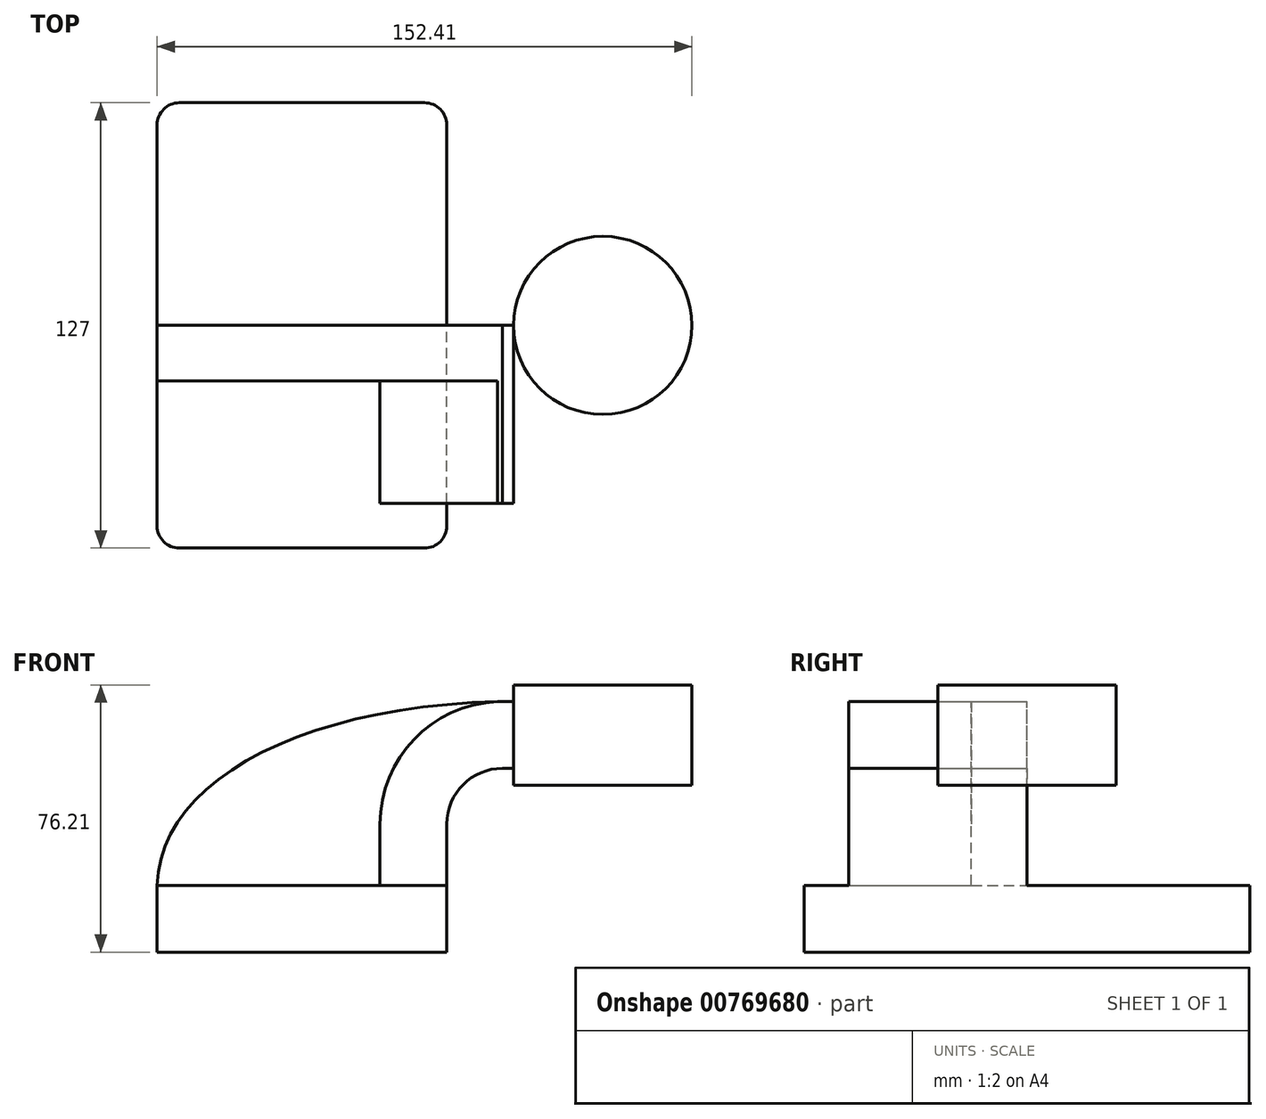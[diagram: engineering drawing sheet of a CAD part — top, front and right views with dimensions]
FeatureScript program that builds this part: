
annotation { "Feature Type Name" : "Feature", "Feature Type Description" : "" }
export const myFeature = defineFeature(function(context is Context, id is Id, definition is map)
    precondition{}
    {
        {
            var Q0;
            Q0=qCreatedBy(makeId("Front.planeOp"),FACE);
            var sketch = newSketch(context, id + "F0", { "sketchPlane" : qUnion([Q0])});
            skLineSegment(sketch, "E0.bottom", {"start": v(41.27, 9.53) * mm, "end": v(-41.28, 9.53) * mm});
            skLineSegment(sketch, "E0.top", {"start": v(41.28, -9.52) * mm, "end": v(-41.27, -9.52) * mm});
            skLineSegment(sketch, "E0.left", {"start": v(41.28, 9.53) * mm, "end": v(41.28, -9.52) * mm});
            skLineSegment(sketch, "E0.right", {"start": v(-41.28, 9.53) * mm, "end": v(-41.27, -9.52) * mm});
            skPoint(sketch, "E0.middle", {"position": v(0, 0) * mm});
            skLineSegment(sketch, "E1", {"start": v(41.27, 9.53) * mm, "end": v(41.27, 27) * mm});
            skArc(sketch, "E2", {"start": v(41.27, 27) * mm, "mid": v(45.92, 38.23) * mm, "end": v(57.15, 42.88) * mm});
            skLineSegment(sketch, "E3", {"start": v(57.15, 42.88) * mm, "end": v(85.72, 42.88) * mm});
            skLineSegment(sketch, "E4.bottom", {"start": v(111.12, 38.1) * mm, "end": v(60.33, 38.1) * mm});
            skLineSegment(sketch, "E4.top", {"start": v(111.12, 66.68) * mm, "end": v(60.33, 66.68) * mm});
            skLineSegment(sketch, "E4.left", {"start": v(111.12, 38.1) * mm, "end": v(111.12, 66.68) * mm});
            skLineSegment(sketch, "E4.right", {"start": v(60.33, 38.1) * mm, "end": v(60.33, 66.68) * mm});
            skPoint(sketch, "E4.middle", {"position": v(85.73, 52.39) * mm});
            skLineSegment(sketch, "E5.0", {"start": v(57.15, 61.93) * mm, "end": v(85.72, 61.93) * mm});
            skArc(sketch, "E5.1", {"start": v(22.23, 27) * mm, "mid": v(32.45, 51.7) * mm, "end": v(57.15, 61.93) * mm});
            skLineSegment(sketch, "E5.2", {"start": v(22.22, 9.53) * mm, "end": v(22.22, 27) * mm});
            skLineSegment(sketch, "E6", {"start": v(85.72, 38.1) * mm, "end": v(85.72, 66.68) * mm});
            skFitSpline(sketch, "E7", {"points": [v(-41.28, 9.53) * mm, v(57.15, 61.93) * mm], "startDerivative": vector(2.07, 88.8) * mm, "endDerivative": vector(171.45, 3.03) * mm});
            skSolve(sketch);
        }
        {
            var Q0;
            Q0=makeQuery(id+"F0.imprint","IMPRINT",FACE,{"disambiguationData":[TD([[makeQuery(id+"F0.imprint","IMPRINT",EDGE,{"derivedFrom":sQuery(id+"F0.wireOp",EDGE,"E0.top")}),-1.0]])]});
            extrude(context, id + "F1", {"entities" : qUnion([Q0]), "endBound" : BoundingType.SYMMETRIC, "depth" : 127 * mm, "offsetDistance" : 25.4 * mm});
        }
        {
            var Q0;
            {var subQ9=sQuery(id+"F0.wireOp",EDGE,"E1");Q0=makeQuery(id+"F0.imprint","IMPRINT",FACE,{"disambiguationData":[TD([[makeQuery(id+"F0.imprint","IMPRINT",EDGE,{"derivedFrom":subQ9}),1.0]])]});}
            extrude(context, id + "F2", {"entities" : qUnion([Q0]), "operationType" : NewBodyOperationType.ADD, "depth" : 50.8 * mm, "offsetDistance" : 25.4 * mm});
        }
        {
            var Q0;
            {var subQ3=sQuery(id+"F0.wireOp",EDGE,"E5.2");Q0=makeQuery(id+"F0.imprint","IMPRINT",FACE,{"disambiguationData":[TD([[makeQuery(id+"F0.imprint","IMPRINT",EDGE,{"derivedFrom":subQ3}),1.0]])]});}
            extrude(context, id + "F3", {"entities" : qUnion([Q0]), "operationType" : NewBodyOperationType.ADD, "depth" : 15.88 * mm, "offsetDistance" : 25.4 * mm});
        }
        {
            var Q0;
            {var subQ4=sQuery(id+"F0.wireOp",EDGE,"E4.left");Q0=makeQuery(id+"F0.imprint","IMPRINT",FACE,{"disambiguationData":[TD([[makeQuery(id+"F0.imprint","IMPRINT",EDGE,{"derivedFrom":subQ4}),1.0]])]});}
            var Q1;
            Q1=sQuery(id+"F0.wireOp",EDGE,"E6");
            revolve(context, id + "F4", {"surfaceOperationType" : NewSurfaceOperationType.NEW, "entities" : qUnion([Q0]), "axis" : qUnion([Q1]), "revolveType" : RevolveType.FULL});
        }
        {
            var Q0;
            Q0=makeQuery(id+"F1.opExtrude","CAP_EDGE",EDGE,{"disambiguationData":[OSD([sQuery(id+"F0.wireOp",EDGE,"E0.left")])],"isStart":false});
            var Q1;
            Q1=makeQuery(id+"F1.opExtrude","CAP_EDGE",EDGE,{"disambiguationData":[OSD([sQuery(id+"F0.wireOp",EDGE,"E0.right")])],"isStart":false});
            var Q2;
            Q2=makeQuery(id+"F1.opExtrude","CAP_EDGE",EDGE,{"disambiguationData":[OSD([sQuery(id+"F0.wireOp",EDGE,"E0.left")])],"isStart":true});
            var Q3;
            Q3=makeQuery(id+"F1.opExtrude","CAP_EDGE",EDGE,{"disambiguationData":[OSD([sQuery(id+"F0.wireOp",EDGE,"E0.right")])],"isStart":true});
            fillet(context, id + "F5", {"entities" : qUnion([Q0, Q1, Q2, Q3]), "radius" : 6.35 * mm, "tangentPropagation" : true, "allowEdgeOverflow" : false});
        }
    });
